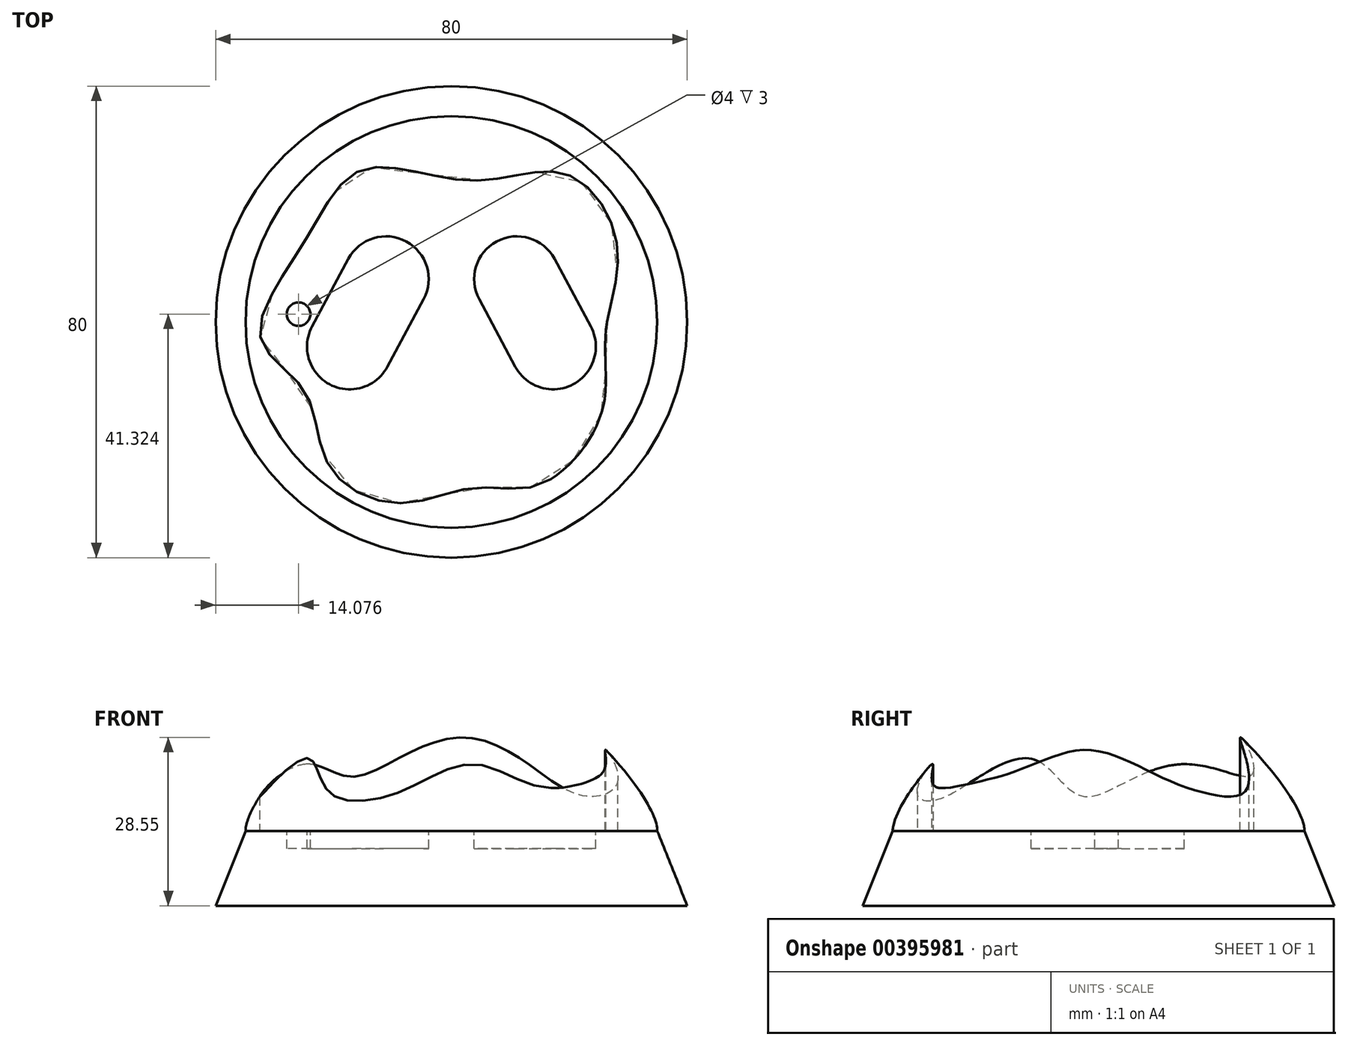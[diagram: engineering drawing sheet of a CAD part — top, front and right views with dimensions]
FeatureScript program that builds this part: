
annotation { "Feature Type Name" : "Feature", "Feature Type Description" : "" }
export const myFeature = defineFeature(function(context is Context, id is Id, definition is map)
    precondition{}
    {
        {
            var Q0;
            Q0=qCreatedBy(makeId("Top.planeOp"),FACE);
            var sketch = newSketch(context, id + "F0", { "sketchPlane" : qUnion([Q0])});
            skCircle(sketch, "E0", {"center": v(0, 0) * mm, "radius": 40 * mm});
            skSolve(sketch);
        }
        {
            var Q0;
            Q0=makeQuery(id+"F0.imprint","IMPRINT",FACE,{"disambiguationData":[TD([[makeQuery(id+"F0.imprint","IMPRINT",EDGE,{"derivedFrom":sQuery(id+"F0.wireOp",EDGE,"E0")}),1.0]])]});
            extrude(context, id + "F1", {"entities" : qUnion([Q0]), "depth" : 12.7 * mm});
        }
        {
            var Q0;
            Q0=makeQuery(id+"F1.opExtrude","CAP_EDGE",EDGE,{"disambiguationData":[OSD([sQuery(id+"F0.wireOp",EDGE,"E0")])],"isStart":false});
            chamfer(context, id + "F2", {"entities" : qUnion([Q0]), "chamferType" : ChamferType.TWO_OFFSETS, "width1" : 5.08 * mm, "oppositeDirection" : false, "width2" : 12.7 * mm, "tangentPropagation" : true});
        }
        {
            var Q0;
            Q0=makeQuery(id+"F1.opExtrude","CAP_FACE",FACE,{"disambiguationData":[OSD([sQuery(id+"F0.wireOp",EDGE,"E0")])],"isStart":false});
            var sketch = newSketch(context, id + "F3", { "sketchPlane" : qUnion([Q0])});
            skFitSpline(sketch, "E1", {"points": [v(-24.65, 14.1) * mm, v(-14.75, 25.98) * mm, v(3.4, 24) * mm, v(19.72, 24.99) * mm, v(28.14, 12.78) * mm, v(26.16, -1.9) * mm, v(25.5, -15.26) * mm, v(14.94, -27.64) * mm, v(3.89, -28.13) * mm, v(-8.81, -30.77) * mm, v(-20.7, -24.5) * mm, v(-24.98, -11.63) * mm, v(-32.4, -2.73) * mm, v(-24.65, 14.1) * mm]});
            skSolve(sketch);
        }
        {
            var Q0;
            Q0=makeQuery(id+"F3.imprint","IMPRINT",FACE,{"disambiguationData":[TD([[makeQuery(id+"F3.imprint","IMPRINT",EDGE,{"derivedFrom":sQuery(id+"F3.wireOp",EDGE,"E1")}),1.0]])]});
            extrude(context, id + "F4", {"entities" : qUnion([Q0]), "operationType" : NewBodyOperationType.ADD, "depth" : 25.4 * mm});
        }
        {
            var Q0;
            Q0=makeQuery(id+"F4.opExtrude","CAP_EDGE",EDGE,{"disambiguationData":[OSD([sQuery(id+"F0.wireOp",EDGE,"E0")])],"isStart":false});
            fillet(context, id + "F5", {"entities" : qUnion([Q0]), "radius" : 25.4 * mm, "tangentPropagation" : true, "rho" : 0.2, "crossSection" : FilletCrossSection.CONIC, "allowEdgeOverflow" : false});
        }
        {
            var Q0;
            Q0=makeQuery(id+"F1.opExtrude","CAP_FACE",FACE,{"disambiguationData":[OSD([sQuery(id+"F0.wireOp",EDGE,"E0")])],"isStart":false});
            var sketch = newSketch(context, id + "F6", { "sketchPlane" : qUnion([Q0])});
            skLineSegment(sketch, "E2", {"start": v(-4.71, 3.85) * mm, "end": v(-10.86, -7.6) * mm});
            skLineSegment(sketch, "E3", {"start": v(-20.67, -10.57) * mm, "end": v(-20.67, -10.57) * mm});
            skLineSegment(sketch, "E4", {"start": v(-23.63, -0.75) * mm, "end": v(-17.49, 10.7) * mm});
            skLineSegment(sketch, "E5", {"start": v(-7.67, 13.66) * mm, "end": v(-7.67, 13.66) * mm});
            skLineSegment(sketch, "E6", {"start": v(4.71, 3.85) * mm, "end": v(10.86, -7.6) * mm});
            skLineSegment(sketch, "E7", {"start": v(20.67, -10.57) * mm, "end": v(20.67, -10.57) * mm});
            skLineSegment(sketch, "E8", {"start": v(23.63, -0.75) * mm, "end": v(17.49, 10.7) * mm});
            skLineSegment(sketch, "E9", {"start": v(7.67, 13.66) * mm, "end": v(7.67, 13.66) * mm});
            skLineSegment(sketch, "E10", {"start": v(0, 0) * mm, "end": v(-1.28, 10.24) * mm});
            skLineSegment(sketch, "E11", {"start": v(0, 0) * mm, "end": v(1.28, 10.24) * mm});
            skLineSegment(sketch, "E12", {"start": v(0, 0) * mm, "end": v(-14.28, -14) * mm});
            skLineSegment(sketch, "E13", {"start": v(0, 0) * mm, "end": v(14.28, -14) * mm});
            skPoint(sketch, "E14.visualSharp", {"position": v(-27.06, -7.14) * mm});
            skArc(sketch, "E14.filletArc", {"start": v(-23.63, -0.75) * mm, "mid": v(-24.19, -6.28) * mm, "end": v(-20.67, -10.57) * mm});
            skPoint(sketch, "E15.visualSharp", {"position": v(-14.06, 17.09) * mm});
            skArc(sketch, "E15.filletArc", {"start": v(-7.67, 13.66) * mm, "mid": v(-13.2, 14.21) * mm, "end": v(-17.49, 10.7) * mm});
            skPoint(sketch, "E16.visualSharp", {"position": v(-14.28, -14) * mm});
            skArc(sketch, "E16.filletArc", {"start": v(-20.67, -10.57) * mm, "mid": v(-15.15, -11.12) * mm, "end": v(-10.86, -7.6) * mm});
            skPoint(sketch, "E17.visualSharp", {"position": v(-1.28, 10.24) * mm});
            skArc(sketch, "E17.filletArc", {"start": v(-4.71, 3.85) * mm, "mid": v(-4.16, 9.37) * mm, "end": v(-7.67, 13.66) * mm});
            skPoint(sketch, "E18.visualSharp", {"position": v(1.28, 10.24) * mm});
            skArc(sketch, "E18.filletArc", {"start": v(7.67, 13.66) * mm, "mid": v(4.16, 9.37) * mm, "end": v(4.71, 3.85) * mm});
            skPoint(sketch, "E19.visualSharp", {"position": v(14.06, 17.09) * mm});
            skArc(sketch, "E19.filletArc", {"start": v(17.49, 10.7) * mm, "mid": v(13.2, 14.21) * mm, "end": v(7.67, 13.66) * mm});
            skPoint(sketch, "E20.visualSharp", {"position": v(14.28, -14) * mm});
            skArc(sketch, "E20.filletArc", {"start": v(10.86, -7.6) * mm, "mid": v(15.15, -11.12) * mm, "end": v(20.67, -10.57) * mm});
            skPoint(sketch, "E21.visualSharp", {"position": v(27.06, -7.14) * mm});
            skArc(sketch, "E21.filletArc", {"start": v(20.67, -10.57) * mm, "mid": v(24.19, -6.28) * mm, "end": v(23.63, -0.75) * mm});
            skLineSegment(sketch, "E22", {"start": v(-14.06, 17.09) * mm, "end": v(-1.28, 10.24) * mm});
            skLineSegment(sketch, "E23", {"start": v(1.28, 10.24) * mm, "end": v(14.06, 17.09) * mm});
            skLineSegment(sketch, "E24", {"start": v(14.28, -14) * mm, "end": v(27.06, -7.14) * mm});
            skLineSegment(sketch, "E25", {"start": v(27.06, -7.14) * mm, "end": v(23.63, -0.75) * mm});
            skLineSegment(sketch, "E26", {"start": v(14.28, -14) * mm, "end": v(10.86, -7.6) * mm});
            skLineSegment(sketch, "E27", {"start": v(1.28, 10.24) * mm, "end": v(4.71, 3.85) * mm});
            skLineSegment(sketch, "E28", {"start": v(14.06, 17.09) * mm, "end": v(17.49, 10.7) * mm});
            skLineSegment(sketch, "E29", {"start": v(-14.06, 17.09) * mm, "end": v(-17.49, 10.7) * mm});
            skLineSegment(sketch, "E30", {"start": v(-1.28, 10.24) * mm, "end": v(-4.71, 3.85) * mm});
            skLineSegment(sketch, "E31", {"start": v(-27.06, -7.14) * mm, "end": v(-23.63, -0.75) * mm});
            skLineSegment(sketch, "E32", {"start": v(-27.06, -7.14) * mm, "end": v(-14.28, -14) * mm});
            skLineSegment(sketch, "E33", {"start": v(-14.28, -14) * mm, "end": v(-10.86, -7.6) * mm});
            skLineSegment(sketch, "E34", {"start": v(-20.67, -10.57) * mm, "end": v(-16.9, -3.52) * mm});
            skLineSegment(sketch, "E35", {"start": v(-16.9, -3.52) * mm, "end": v(-25.92, 1.32) * mm});
            skCircle(sketch, "E36", {"center": v(-25.92, 1.32) * mm, "radius": 2 * mm});
            skSolve(sketch);
        }
        {
            var Q0;
            Q0=makeQuery(id+"F6.imprint","IMPRINT",FACE,{"disambiguationData":[TD([[makeQuery(id+"F6.imprint","IMPRINT",EDGE,{"derivedFrom":sQuery(id+"F6.wireOp",EDGE,"E36")}),1.0]])]});
            var Q1;
            Q1=makeQuery(id+"F6.imprint","IMPRINT",FACE,{"disambiguationData":[TD([[makeQuery(id+"F6.imprint","IMPRINT",EDGE,{"derivedFrom":sQuery(id+"F6.wireOp",EDGE,"E2")}),-1.0]])]});
            var Q2;
            {var subQ0=sQuery(id+"F6.wireOp",EDGE,"E14.filletArc");Q2=makeQuery(id+"F6.imprint","IMPRINT",FACE,{"disambiguationData":[TD([[makeQuery(id+"F6.imprint","IMPRINT",EDGE,{"derivedFrom":subQ0}),1.0]])]});}
            var Q3;
            Q3=makeQuery(id+"F6.imprint","IMPRINT",FACE,{"disambiguationData":[TD([[makeQuery(id+"F6.imprint","IMPRINT",EDGE,{"derivedFrom":sQuery(id+"F6.wireOp",EDGE,"E6")}),1.0]])]});
            extrude(context, id + "F7", {"entities" : qUnion([Q0, Q1, Q2, Q3]), "operationType" : NewBodyOperationType.REMOVE, "oppositeDirection" : true, "depth" : 3 * mm});
        }
    });
